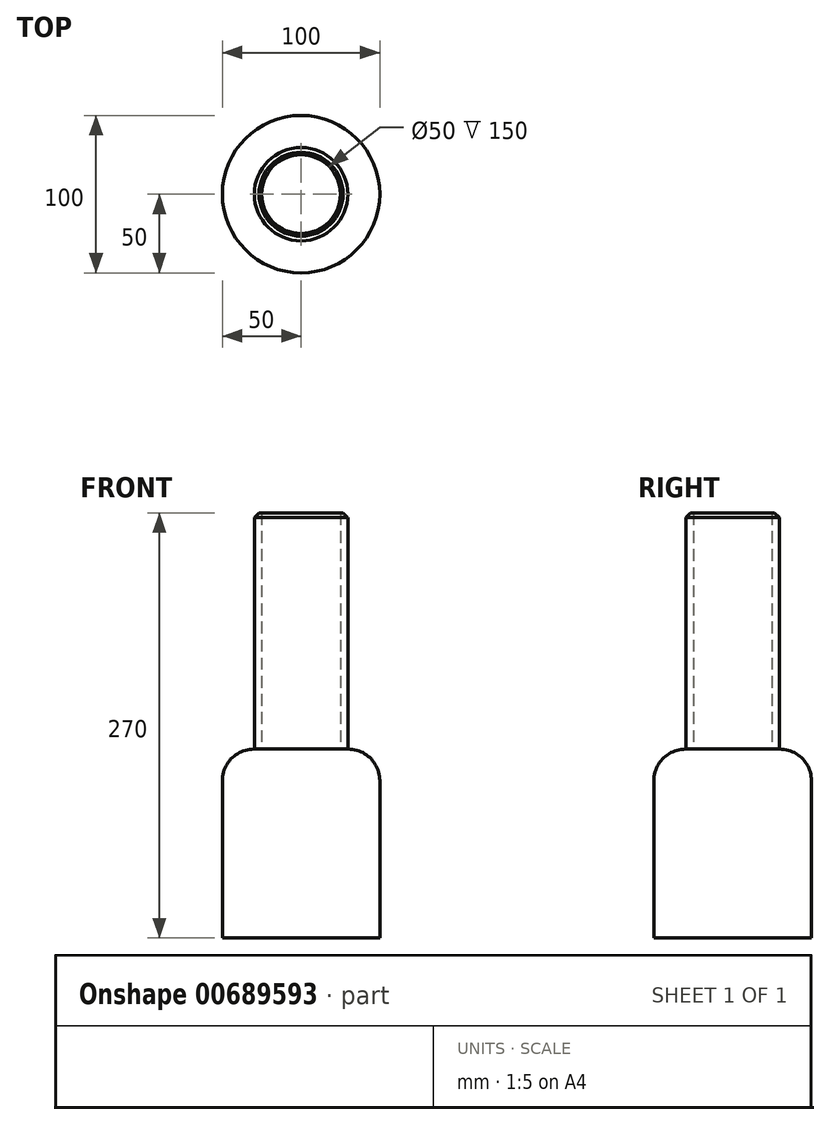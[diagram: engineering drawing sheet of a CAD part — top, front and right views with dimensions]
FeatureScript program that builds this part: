
annotation { "Feature Type Name" : "Feature", "Feature Type Description" : "" }
export const myFeature = defineFeature(function(context is Context, id is Id, definition is map)
    precondition{}
    {
        {
            var Q0;
            Q0=qCreatedBy(makeId("Top.planeOp"),FACE);
            var sketch = newSketch(context, id + "F0", { "sketchPlane" : qUnion([Q0])});
            skCircle(sketch, "E0", {"center": v(0, 0) * mm, "radius": 50 * mm});
            skSolve(sketch);
        }
        {
            var Q0;
            Q0=makeQuery(id+"F0.imprint","IMPRINT",FACE,{"disambiguationData":[TD([[makeQuery(id+"F0.imprint","IMPRINT",EDGE,{"derivedFrom":sQuery(id+"F0.wireOp",EDGE,"E0")}),1.0]])]});
            extrude(context, id + "F1", {"entities" : qUnion([Q0]), "depth" : 120 * mm, "offsetDistance" : 25.4 * mm});
        }
        {
            var Q0;
            Q0=makeQuery(id+"F1.opExtrude","CAP_FACE",FACE,{"disambiguationData":[OSD([sQuery(id+"F0.wireOp",EDGE,"E0")])],"isStart":false});
            var sketch = newSketch(context, id + "F2", { "sketchPlane" : qUnion([Q0])});
            skCircle(sketch, "E1", {"center": v(0, 0) * mm, "radius": 25 * mm});
            skSolve(sketch);
        }
        {
            var Q0;
            Q0=makeQuery(id+"F2.imprint","IMPRINT",FACE,{"disambiguationData":[TD([[makeQuery(id+"F2.imprint","IMPRINT",EDGE,{"derivedFrom":sQuery(id+"F2.wireOp",EDGE,"E1")}),1.0]])]});
            extrude(context, id + "F3", {"entities" : qUnion([Q0]), "depth" : 150 * mm, "offsetDistance" : 25.4 * mm});
        }
        {
            var Q0;
            Q0=makeQuery(id+"F1.opExtrude","CAP_EDGE",EDGE,{"disambiguationData":[OSD([sQuery(id+"F0.wireOp",EDGE,"E0")])],"isStart":false});
            fillet(context, id + "F4", {"entities" : qUnion([Q0]), "radius" : 20 * mm, "tangentPropagation" : true, "allowEdgeOverflow" : false});
        }
        {
            var Q0;
            Q0=makeQuery(id+"F3.opExtrude","CAP_FACE",FACE,{"disambiguationData":[OSD([sQuery(id+"F2.wireOp",EDGE,"E1")])],"isStart":false});
            var sketch = newSketch(context, id + "F5", { "sketchPlane" : qUnion([Q0])});
            skCircle(sketch, "E2", {"center": v(0, 0) * mm, "radius": 29.67 * mm});
            skSolve(sketch);
        }
        {
            var Q0;
            Q0=makeQuery(id+"F5.imprint","IMPRINT",FACE,{"disambiguationData":[TD([[makeQuery(id+"F5.imprint","IMPRINT",EDGE,{"derivedFrom":sQuery(id+"F5.wireOp",EDGE,"E2")}),1.0]])]});
            extrude(context, id + "F6", {"entities" : qUnion([Q0]), "depth" : -150 * mm, "offsetDistance" : 25.4 * mm});
        }
        {
            var Q0;
            Q0=makeQuery(id+"F6.opExtrude","CAP_EDGE",EDGE,{"disambiguationData":[OSD([sQuery(id+"F5.wireOp",EDGE,"E2")])],"isStart":true});
            chamfer(context, id + "F7", {"entities" : qUnion([Q0]), "width" : 3 * mm, "tangentPropagation" : true});
        }
    });
